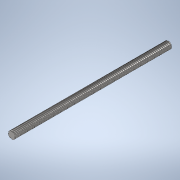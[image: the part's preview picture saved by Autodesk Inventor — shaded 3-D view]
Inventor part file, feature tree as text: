
AUTODESK INVENTOR PART (.ipt)
format: ipt  version: 2020 (Build 240168000, 168)  size: 934,400 bytes
history: native  units: mm
features: sketch x2, extrude x1, helix x1, pattern_circular x1
ambient origin geometry x8: Origin, YZ Plane, XZ Plane, XY Plane, X Axis, Y Axis, Z Axis, Center Point
bodies: Solid1 (feature_tree)
feature tree (5):
  extrude  "Extrusion1"  Depth=8.0mm TaperAngle=0.0deg
  helix  "Coil1"  [1 undecoded]
  pattern_circular  "Circular Pattern1"  Count=4 Angle=360.0deg
  sketch  "Sketch1"  dims[d0=8.0mm d1=180.0mm d2=0.0mm d3=1.0mm]
  sketch  "Sketch2"  dims[d4=3.8mm d5=8.0mm d6=10.0mm d7=225.0mm d8=0.0mm d9=90.0deg d10=90.0deg d11=0.0mm d12=0.0mm d13=40.0mm d14=360.0deg]
note: 1 required parameter value undecoded (feature->parameter linkage not recoverable at this tier; creation-order binding heuristic only, values carry confidence <= 0.55)
